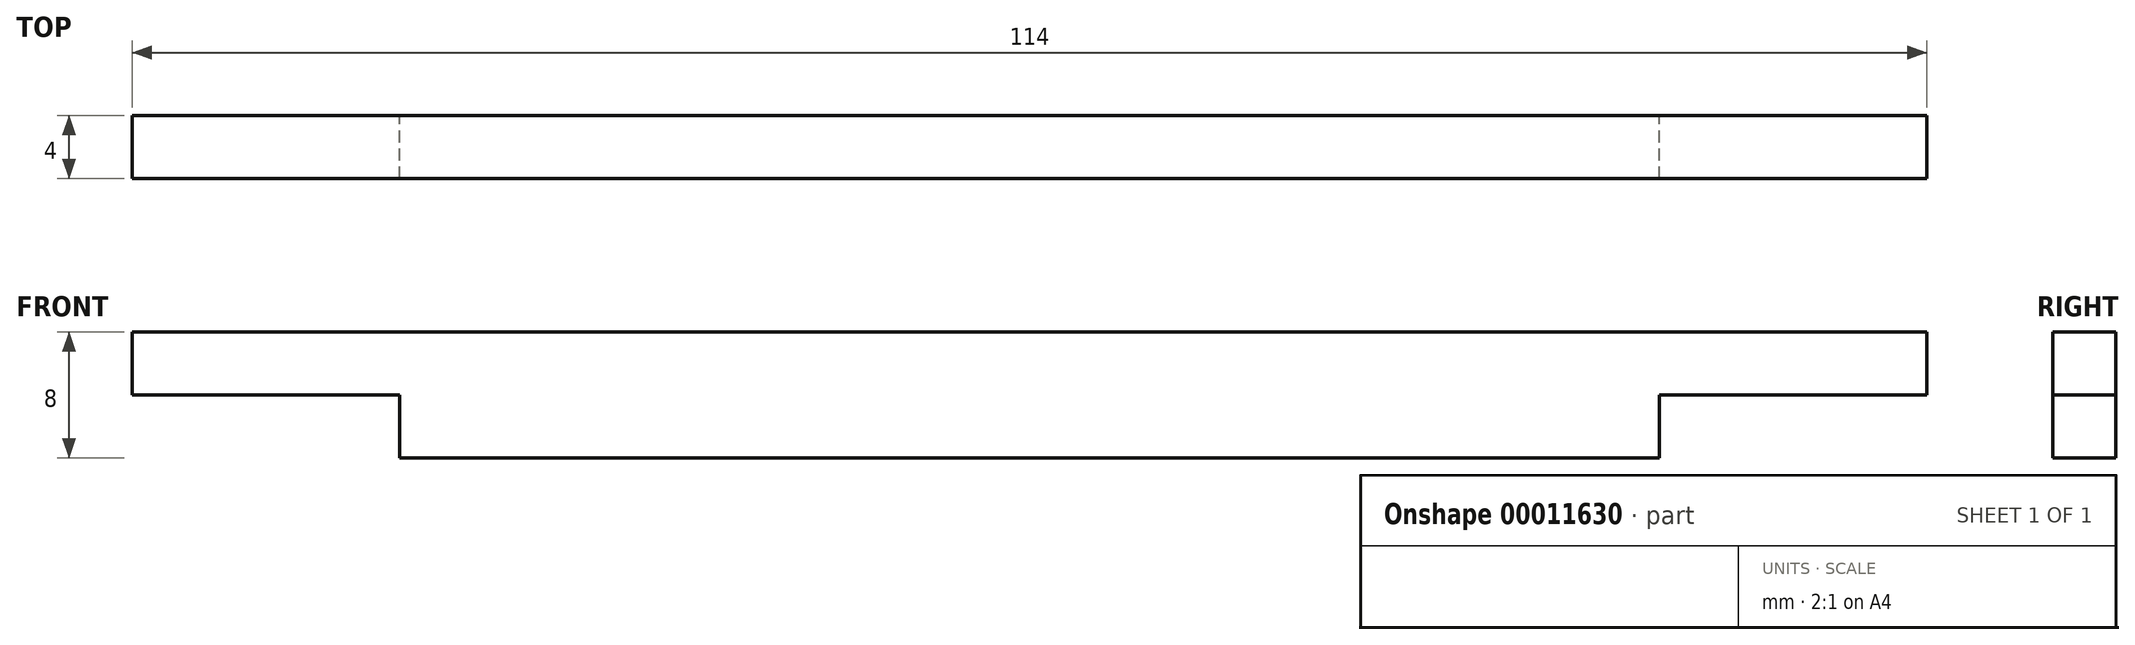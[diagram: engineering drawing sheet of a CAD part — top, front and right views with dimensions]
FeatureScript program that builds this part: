
annotation { "Feature Type Name" : "Feature", "Feature Type Description" : "" }
export const myFeature = defineFeature(function(context is Context, id is Id, definition is map)
    precondition{}
    {
        {
            var Q0;
            Q0=qCreatedBy(makeId("Front.planeOp"),FACE);
            var sketch = newSketch(context, id + "F0", { "sketchPlane" : qUnion([Q0])});
            skLineSegment(sketch, "E0", {"start": v(-57, 0) * mm, "end": v(57, 0) * mm});
            skLineSegment(sketch, "E1", {"start": v(57, 0) * mm, "end": v(57, -4) * mm});
            skLineSegment(sketch, "E2", {"start": v(57, -4) * mm, "end": v(40, -4) * mm});
            skLineSegment(sketch, "E3", {"start": v(40, -4) * mm, "end": v(40, -8) * mm});
            skLineSegment(sketch, "E4", {"start": v(40, -8) * mm, "end": v(-40, -8) * mm});
            skLineSegment(sketch, "E5", {"start": v(-40, -8) * mm, "end": v(-40, -4) * mm});
            skLineSegment(sketch, "E6", {"start": v(-40, -4) * mm, "end": v(-57, -4) * mm});
            skLineSegment(sketch, "E7", {"start": v(-57, -4) * mm, "end": v(-57, 0) * mm});
            skSolve(sketch);
        }
        {
            var Q0;
            Q0=makeQuery(id+"F0.imprint","IMPRINT",FACE,{"disambiguationData":[TD([[makeQuery(id+"F0.imprint","IMPRINT",EDGE,{"derivedFrom":sQuery(id+"F0.wireOp",EDGE,"E0")}),-1.0]])]});
            extrude(context, id + "F1", {"entities" : qUnion([Q0]), "endBound" : BoundingType.SYMMETRIC, "depth" : 4 * mm});
        }
    });
